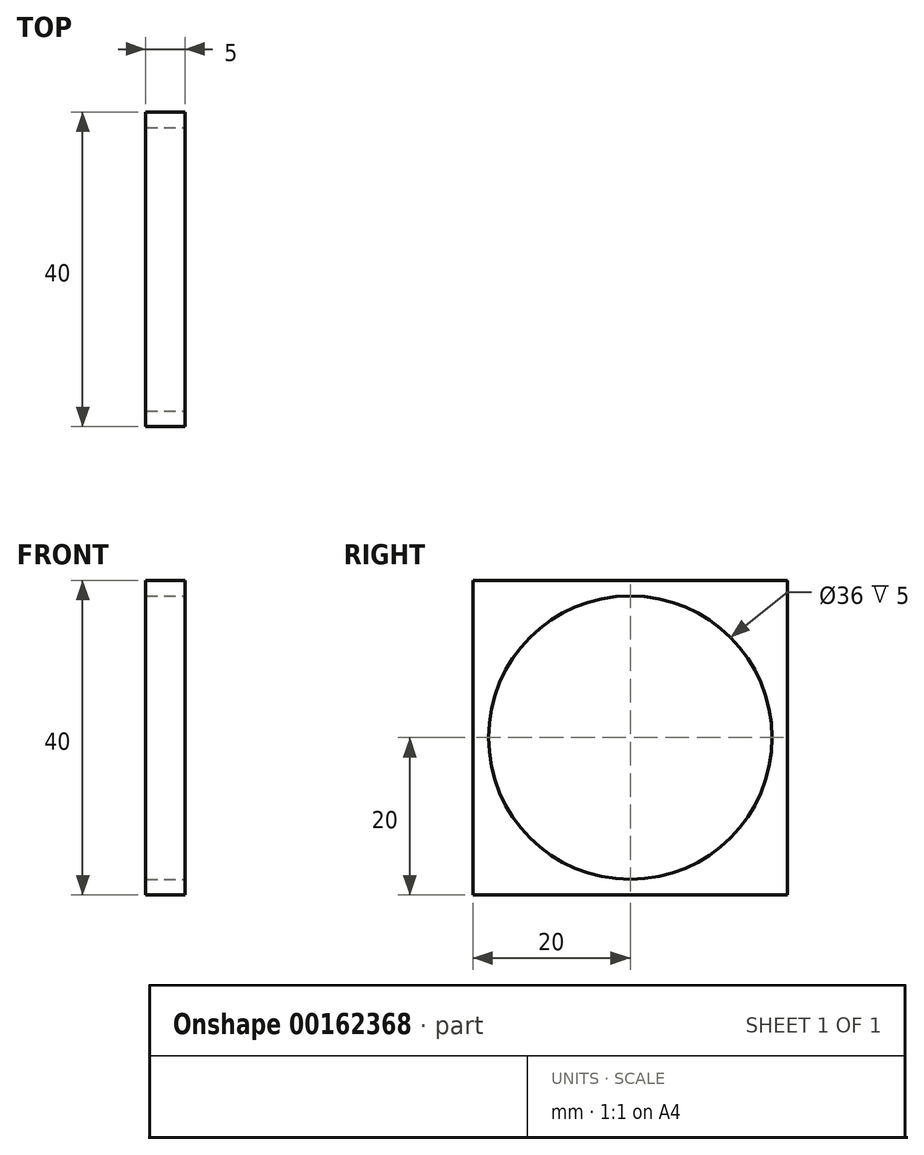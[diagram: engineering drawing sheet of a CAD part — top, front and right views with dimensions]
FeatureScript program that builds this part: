
annotation { "Feature Type Name" : "Feature", "Feature Type Description" : "" }
export const myFeature = defineFeature(function(context is Context, id is Id, definition is map)
    precondition{}
    {
        {
            var Q0;
            Q0=qCreatedBy(makeId("Right.planeOp"),FACE);
            var sketch = newSketch(context, id + "F0", { "sketchPlane" : qUnion([Q0])});
            skLineSegment(sketch, "E0.bottom", {"start": v(0, 0) * mm, "end": v(40, 0) * mm});
            skLineSegment(sketch, "E0.top", {"start": v(0, 40) * mm, "end": v(40, 40) * mm});
            skLineSegment(sketch, "E0.left", {"start": v(0, 0) * mm, "end": v(0, 40) * mm});
            skLineSegment(sketch, "E0.right", {"start": v(40, 0) * mm, "end": v(40, 40) * mm});
            skSolve(sketch);
        }
        {
            var Q0;
            Q0=makeQuery(id+"F0.imprint","IMPRINT",FACE,{"disambiguationData":[TD([[makeQuery(id+"F0.imprint","IMPRINT",EDGE,{"derivedFrom":sQuery(id+"F0.wireOp",EDGE,"E0.bottom")}),1.0]])]});
            extrude(context, id + "F1", {"entities" : qUnion([Q0]), "oppositeDirection" : true, "depth" : 5 * mm});
        }
        {
            var Q0;
            Q0=makeQuery(id+"F1.opExtrude","CAP_FACE",FACE,{"disambiguationData":[OSD([sQuery(id+"F0.wireOp",EDGE,"E0.bottom"),sQuery(id+"F0.wireOp",EDGE,"E0.top"),sQuery(id+"F0.wireOp",EDGE,"E0.left"),sQuery(id+"F0.wireOp",EDGE,"E0.right")])],"isStart":true});
            var sketch = newSketch(context, id + "F2", { "sketchPlane" : qUnion([Q0])});
            skCircle(sketch, "E1", {"center": v(20, 20) * mm, "radius": 18 * mm});
            skSolve(sketch);
        }
        {
            var Q0;
            Q0 = qSketchRegion(id + "F2", true);
            extrude(context, id + "F3", {"entities" : qUnion([Q0]), "operationType" : NewBodyOperationType.REMOVE, "endBound" : BoundingType.UP_TO_NEXT, "oppositeDirection" : true, "depth" : 25 * mm});
        }
        {
            var Q0;
            Q0=qCreatedBy(makeId("Right.planeOp"),FACE);
            cPlane(context, id + "F4", {"entities" : qUnion([Q0]), "cplaneType" : CPlaneType.OFFSET, "offset" : 30 * mm, "oppositeDirection" : true, "width" : 150 * mm, "height" : 150 * mm});
        }
    });
